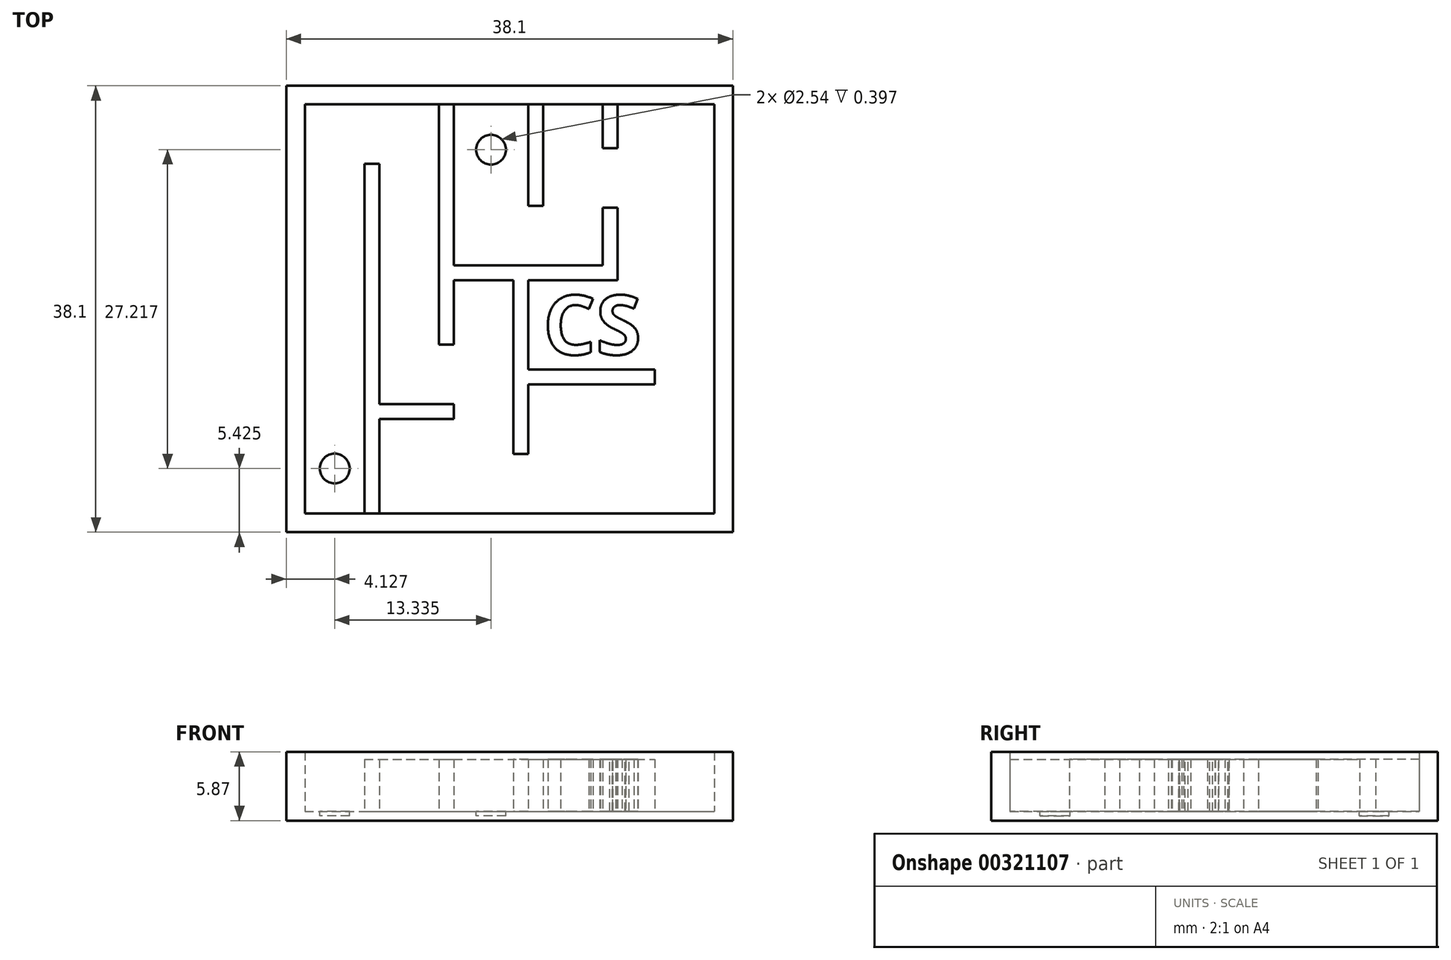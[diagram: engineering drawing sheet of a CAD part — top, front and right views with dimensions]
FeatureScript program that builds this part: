
annotation { "Feature Type Name" : "Feature", "Feature Type Description" : "" }
export const myFeature = defineFeature(function(context is Context, id is Id, definition is map)
    precondition{}
    {
        {
            var Q0;
            Q0=qCreatedBy(makeId("Top.planeOp"),FACE);
            var sketch = newSketch(context, id + "F0", { "sketchPlane" : qUnion([Q0])});
            skLineSegment(sketch, "E0.bottom", {"start": v(-37.93, 25.44) * mm, "end": v(0.17, 25.44) * mm});
            skLineSegment(sketch, "E0.top", {"start": v(-37.93, -12.66) * mm, "end": v(0.17, -12.66) * mm});
            skLineSegment(sketch, "E0.left", {"start": v(-37.93, 25.44) * mm, "end": v(-37.93, -12.66) * mm});
            skLineSegment(sketch, "E0.right", {"start": v(0.17, 25.44) * mm, "end": v(0.17, -12.66) * mm});
            skSolve(sketch);
        }
        {
            var Q0;
            Q0=makeQuery(id+"F0.imprint","IMPRINT",FACE,{"disambiguationData":[TD([[makeQuery(id+"F0.imprint","IMPRINT",EDGE,{"derivedFrom":sQuery(id+"F0.wireOp",EDGE,"E0.bottom")}),-1.0]])]});
            extrude(context, id + "F1", {"entities" : qUnion([Q0]), "depth" : 0.8 * mm});
        }
        {
            var Q0;
            Q0=makeQuery(id+"F1.opExtrude","CAP_FACE",FACE,{"disambiguationData":[OSD([sQuery(id+"F0.wireOp",EDGE,"E0.bottom"),sQuery(id+"F0.wireOp",EDGE,"E0.top"),sQuery(id+"F0.wireOp",EDGE,"E0.left"),sQuery(id+"F0.wireOp",EDGE,"E0.right")])],"isStart":false});
            var sketch = newSketch(context, id + "F2", { "sketchPlane" : qUnion([Q0])});
            skLineSegment(sketch, "E1.0", {"start": v(-36.34, 23.85) * mm, "end": v(-1.42, 23.85) * mm});
            skLineSegment(sketch, "E2.0", {"start": v(-36.34, 23.85) * mm, "end": v(-36.34, -11.08) * mm});
            skLineSegment(sketch, "E3.0", {"start": v(-1.42, 23.85) * mm, "end": v(-1.42, -11.08) * mm});
            skLineSegment(sketch, "E4.0", {"start": v(-36.34, -11.08) * mm, "end": v(-1.42, -11.08) * mm});
            skSolve(sketch);
        }
        {
            var Q0;
            Q0=makeQuery(id+"F2.imprint","IMPRINT",FACE,{"disambiguationData":[TD([[makeQuery(id+"F2.imprint","IMPRINT",EDGE,{"derivedFrom":sQuery(id+"F2.wireOp",EDGE,"E1.0")}),1.0]])]});
            extrude(context, id + "F3", {"entities" : qUnion([Q0]), "operationType" : NewBodyOperationType.ADD, "depth" : 5.08 * mm});
        }
        {
            var Q0;
            Q0=makeQuery(id+"F1.opExtrude","CAP_FACE",FACE,{"disambiguationData":[OSD([sQuery(id+"F0.wireOp",EDGE,"E0.bottom"),sQuery(id+"F0.wireOp",EDGE,"E0.top"),sQuery(id+"F0.wireOp",EDGE,"E0.left"),sQuery(id+"F0.wireOp",EDGE,"E0.right")])],"isStart":false});
            var sketch = newSketch(context, id + "F4", { "sketchPlane" : qUnion([Q0])});
            skLineSegment(sketch, "E5.bottom", {"start": v(-31.26, -11.08) * mm, "end": v(-30, -11.08) * mm});
            skLineSegment(sketch, "E5.top", {"start": v(-31.26, 18.77) * mm, "end": v(-30, 18.77) * mm});
            skLineSegment(sketch, "E5.left", {"start": v(-31.26, -11.08) * mm, "end": v(-31.26, 18.77) * mm});
            skLineSegment(sketch, "E5.right", {"start": v(-30, -11.08) * mm, "end": v(-30, -3) * mm});
            skLineSegment(sketch, "E6.bottom", {"start": v(-24.91, 23.85) * mm, "end": v(-23.64, 23.85) * mm});
            skLineSegment(sketch, "E6.top", {"start": v(-24.91, 3.36) * mm, "end": v(-23.64, 3.36) * mm});
            skLineSegment(sketch, "E6.left", {"start": v(-24.91, 23.85) * mm, "end": v(-24.91, 3.36) * mm});
            skLineSegment(sketch, "E6.right", {"start": v(-23.64, 23.85) * mm, "end": v(-23.64, 10.12) * mm});
            skLineSegment(sketch, "E7.bottom", {"start": v(-23.64, 8.85) * mm, "end": v(-18.56, 8.85) * mm});
            skLineSegment(sketch, "E7.top", {"start": v(-23.64, 10.12) * mm, "end": v(-10.94, 10.12) * mm});
            skLineSegment(sketch, "E7.right", {"start": v(-9.67, 8.85) * mm, "end": v(-9.67, 10.12) * mm});
            skLineSegment(sketch, "E8.top", {"start": v(-17.3, -6) * mm, "end": v(-18.56, -6) * mm});
            skLineSegment(sketch, "E8.left", {"start": v(-17.3, 8.85) * mm, "end": v(-17.3, 1.23) * mm});
            skLineSegment(sketch, "E8.right", {"start": v(-18.56, 8.85) * mm, "end": v(-18.56, -6) * mm});
            skLineSegment(sketch, "E9.bottom", {"start": v(-30, -1.72) * mm, "end": v(-23.64, -1.72) * mm});
            skLineSegment(sketch, "E9.top", {"start": v(-30, -3) * mm, "end": v(-23.64, -3) * mm});
            skLineSegment(sketch, "E9.right", {"start": v(-23.64, -1.72) * mm, "end": v(-23.64, -3) * mm});
            skLineSegment(sketch, "E10.bottom", {"start": v(-17.3, 1.23) * mm, "end": v(-6.5, 1.23) * mm});
            skLineSegment(sketch, "E10.top", {"start": v(-17.3, -0.04) * mm, "end": v(-6.5, -0.04) * mm});
            skLineSegment(sketch, "E10.right", {"start": v(-6.5, 1.23) * mm, "end": v(-6.5, -0.04) * mm});
            skLineSegment(sketch, "E11.bottom", {"start": v(-17.3, 23.85) * mm, "end": v(-16.02, 23.85) * mm});
            skLineSegment(sketch, "E11.top", {"start": v(-17.3, 15.2) * mm, "end": v(-16.02, 15.2) * mm});
            skLineSegment(sketch, "E11.left", {"start": v(-17.3, 23.85) * mm, "end": v(-17.3, 15.2) * mm});
            skLineSegment(sketch, "E11.right", {"start": v(-16.02, 23.85) * mm, "end": v(-16.02, 15.2) * mm});
            skLineSegment(sketch, "E12.trimOffspring", {"start": v(-23.64, 8.85) * mm, "end": v(-23.64, 3.36) * mm});
            skLineSegment(sketch, "E13.trimOffspring", {"start": v(-17.3, 8.85) * mm, "end": v(-9.67, 8.85) * mm});
            skLineSegment(sketch, "E14.trimOffspring", {"start": v(-17.3, -0.04) * mm, "end": v(-17.3, -6) * mm});
            skLineSegment(sketch, "E15", {"start": v(-10.94, 15.03) * mm, "end": v(-9.67, 15.03) * mm});
            skLineSegment(sketch, "E16", {"start": v(-9.67, 15.03) * mm, "end": v(-9.67, 10.12) * mm});
            skLineSegment(sketch, "E17", {"start": v(-10.94, 15.03) * mm, "end": v(-10.94, 10.12) * mm});
            skLineSegment(sketch, "E18", {"start": v(-10.94, 23.85) * mm, "end": v(-10.94, 20.1) * mm});
            skLineSegment(sketch, "E19", {"start": v(-10.94, 20.1) * mm, "end": v(-9.67, 20.1) * mm});
            skLineSegment(sketch, "E20", {"start": v(-9.67, 20.1) * mm, "end": v(-9.67, 23.85) * mm});
            skLineSegment(sketch, "E21.trimOffspring", {"start": v(-30, -1.72) * mm, "end": v(-30, 18.77) * mm});
            skSolve(sketch);
        }
        {
            var Q0;
            Q0=makeQuery(id+"F4.imprint","IMPRINT",FACE,{"disambiguationData":[TD([[makeQuery(id+"F4.imprint","IMPRINT",EDGE,{"derivedFrom":sQuery(id+"F4.wireOp",EDGE,"E5.bottom")}),1.0]])]});
            var Q1;
            Q1=makeQuery(id+"F4.imprint","IMPRINT",FACE,{"disambiguationData":[TD([[makeQuery(id+"F4.imprint","IMPRINT",EDGE,{"derivedFrom":sQuery(id+"F4.wireOp",EDGE,"E6.bottom")}),-1.0]])]});
            var Q2;
            Q2=makeQuery(id+"F4.imprint","IMPRINT",FACE,{"disambiguationData":[TD([[makeQuery(id+"F4.imprint","IMPRINT",EDGE,{"derivedFrom":sQuery(id+"F4.wireOp",EDGE,"E11.bottom")}),-1.0]])]});
            var Q3;
            {var subQ0=sQuery(id+"F4.wireOp",EDGE,"E18");Q3=makeQuery(id+"F4.imprint","IMPRINT",FACE,{"disambiguationData":[TD([[makeQuery(id+"F4.imprint","IMPRINT",EDGE,{"derivedFrom":subQ0}),1.0]])]});}
            extrude(context, id + "F5", {"entities" : qUnion([Q0, Q1, Q2, Q3]), "operationType" : NewBodyOperationType.ADD, "depth" : 4.44 * mm});
        }
        {
            var Q0;
            Q0=makeQuery(id+"F1.opExtrude","CAP_FACE",FACE,{"disambiguationData":[OSD([sQuery(id+"F0.wireOp",EDGE,"E0.bottom"),sQuery(id+"F0.wireOp",EDGE,"E0.top"),sQuery(id+"F0.wireOp",EDGE,"E0.left"),sQuery(id+"F0.wireOp",EDGE,"E0.right")])],"isStart":false});
            var sketch = newSketch(context, id + "F6", { "sketchPlane" : qUnion([Q0])});
            skLineSegment(sketch, "E22", {"start": v(-36.34, -11.08) * mm, "end": v(-31.26, -11.08) * mm});
            skCircle(sketch, "E23", {"center": v(-33.8, -7.23) * mm, "radius": 1.27 * mm});
            skPoint(sketch, "E23.centerSnap0", {"position": v(-33.8, -11.08) * mm});
            skLineSegment(sketch, "E24", {"start": v(-23.64, 23.85) * mm, "end": v(-17.3, 23.85) * mm});
            skCircle(sketch, "E25", {"center": v(-20.47, 19.98) * mm, "radius": 1.27 * mm});
            skPoint(sketch, "E25.centerSnap0", {"position": v(-20.47, 23.85) * mm});
            skSolve(sketch);
        }
        {
            var Q0;
            Q0=makeQuery(id+"F6.imprint","IMPRINT",FACE,{"disambiguationData":[TD([[makeQuery(id+"F6.imprint","IMPRINT",EDGE,{"derivedFrom":sQuery(id+"F6.wireOp",EDGE,"E23")}),1.0]])]});
            var Q1;
            Q1=makeQuery(id+"F6.imprint","IMPRINT",FACE,{"disambiguationData":[TD([[makeQuery(id+"F6.imprint","IMPRINT",EDGE,{"derivedFrom":sQuery(id+"F6.wireOp",EDGE,"E25")}),1.0]])]});
            extrude(context, id + "F7", {"entities" : qUnion([Q0, Q1]), "operationType" : NewBodyOperationType.REMOVE, "oppositeDirection" : true, "depth" : 0.4 * mm});
        }
        {
            var Q0;
            Q0=makeQuery(id+"F1.opExtrude","CAP_FACE",FACE,{"disambiguationData":[OSD([sQuery(id+"F0.wireOp",EDGE,"E0.bottom"),sQuery(id+"F0.wireOp",EDGE,"E0.top"),sQuery(id+"F0.wireOp",EDGE,"E0.left"),sQuery(id+"F0.wireOp",EDGE,"E0.right")])],"isStart":false});
            var sketch = newSketch(context, id + "F8", { "sketchPlane" : qUnion([Q0])});
            skText(sketch, "E26", { "text": "CS", "fontName": "OpenSans-Bold.ttf"});
            const initialGuessF8  = {"E26": [-0.01602, 0.0025, 1, 0, 0.00508]};
            skSetInitialGuess(sketch, initialGuessF8);
            skSolve(sketch);
        }
        {
            var Q0;
            Q0=makeQuery(id+"F8.imprint","IMPRINT",FACE,{"disambiguationData":[TD([[makeQuery(id+"F8.imprint","IMPRINT",EDGE,{"derivedFrom":sQuery(id+"F8.wireOp",EDGE,"E26.sketch_text.stroke-0")}),-1.0]])]});
            var Q1;
            Q1=makeQuery(id+"F8.imprint","IMPRINT",FACE,{"disambiguationData":[TD([[makeQuery(id+"F8.imprint","IMPRINT",EDGE,{"derivedFrom":sQuery(id+"F8.wireOp",EDGE,"E26.sketch_text.stroke-15")}),-1.0]])]});
            extrude(context, id + "F9", {"entities" : qUnion([Q0, Q1]), "operationType" : NewBodyOperationType.ADD, "depth" : 4.44 * mm});
        }
    });
